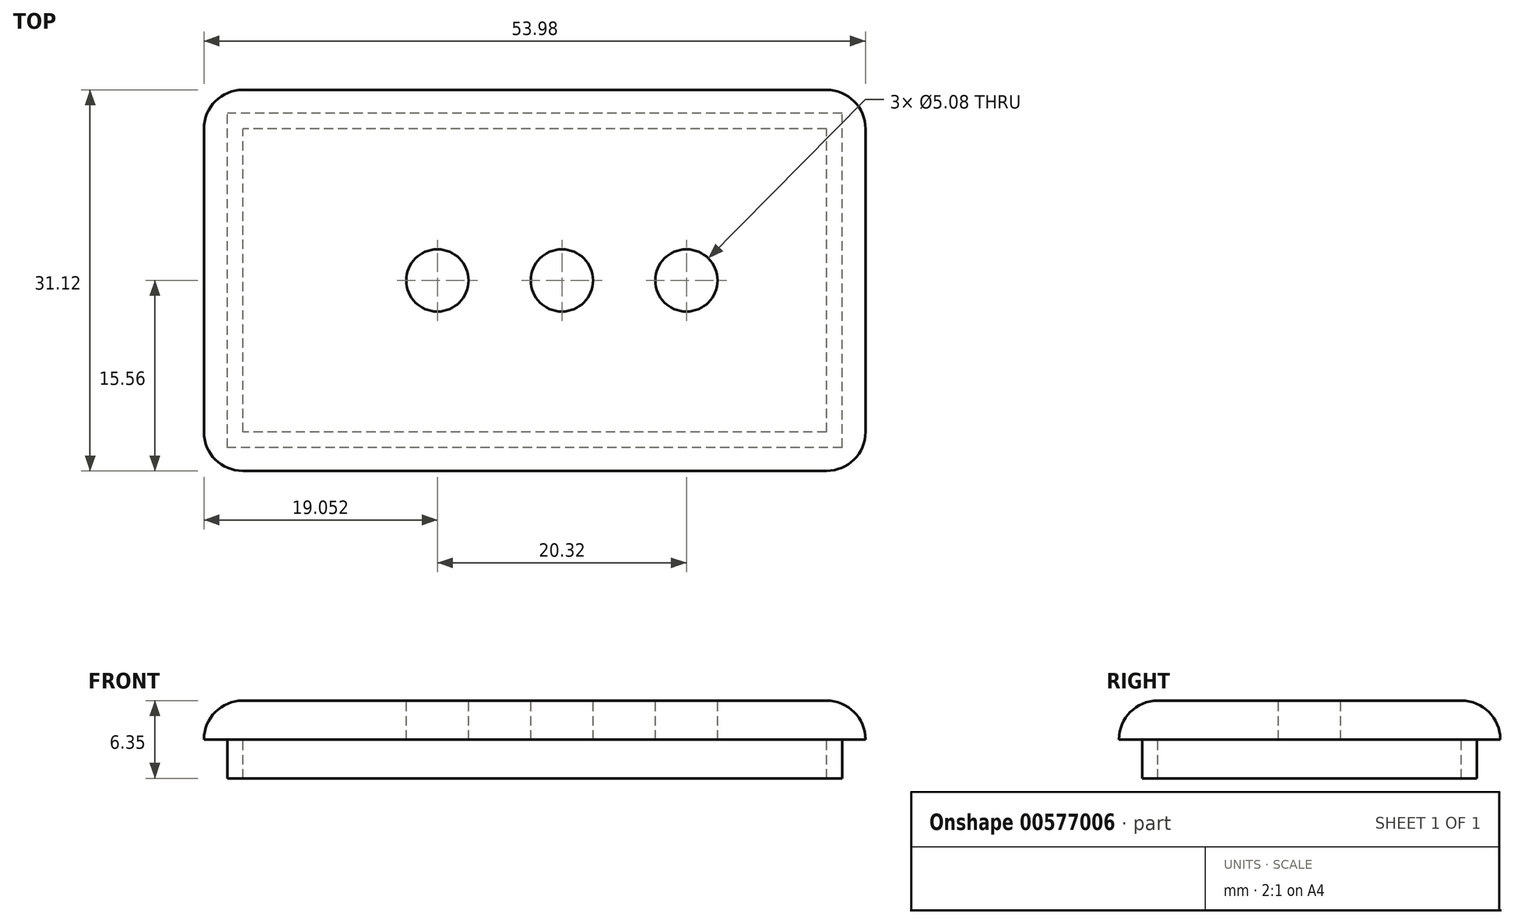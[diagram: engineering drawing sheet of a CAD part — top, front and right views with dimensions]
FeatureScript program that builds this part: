
annotation { "Feature Type Name" : "Feature", "Feature Type Description" : "" }
export const myFeature = defineFeature(function(context is Context, id is Id, definition is map)
    precondition{}
    {
        {
            var Q0;
            Q0=qCreatedBy(makeId("Top.planeOp"),FACE);
            var sketch = newSketch(context, id + "F0", { "sketchPlane" : qUnion([Q0])});
            skLineSegment(sketch, "E0.bottom", {"start": v(26.99, 15.56) * mm, "end": v(-26.99, 15.56) * mm});
            skLineSegment(sketch, "E0.top", {"start": v(26.99, -15.56) * mm, "end": v(-26.99, -15.56) * mm});
            skLineSegment(sketch, "E0.left", {"start": v(26.99, 15.56) * mm, "end": v(26.99, -15.56) * mm});
            skLineSegment(sketch, "E0.right", {"start": v(-26.99, 15.56) * mm, "end": v(-26.99, -15.56) * mm});
            skPoint(sketch, "E0.middle", {"position": v(0, 0) * mm});
            skSolve(sketch);
        }
        {
            var Q0;
            Q0 = qSketchRegion(id + "F0", true);
            extrude(context, id + "F1", {"entities" : qUnion([Q0]), "depth" : 3.17 * mm, "offsetDistance" : 25.4 * mm});
        }
        {
            var Q0;
            Q0=makeQuery(id+"F1.opExtrude","CAP_EDGE",EDGE,{"disambiguationData":[OSD([sQuery(id+"F0.wireOp",EDGE,"E0.top")])],"isStart":false});
            var Q1;
            Q1=makeQuery(id+"F1.opExtrude","CAP_EDGE",EDGE,{"disambiguationData":[OSD([sQuery(id+"F0.wireOp",EDGE,"E0.right")])],"isStart":false});
            var Q2;
            Q2=makeQuery(id+"F1.opExtrude","CAP_EDGE",EDGE,{"disambiguationData":[OSD([sQuery(id+"F0.wireOp",EDGE,"E0.bottom")])],"isStart":false});
            var Q3;
            Q3=makeQuery(id+"F1.opExtrude","CAP_EDGE",EDGE,{"disambiguationData":[OSD([sQuery(id+"F0.wireOp",EDGE,"E0.left")])],"isStart":false});
            var Q4;
            Q4=makeQuery(id+"F1.opExtrude","SWEPT_EDGE",EDGE,{"disambiguationData":[OSD([sQuery(id+"F0.wireOp",EDGE,"E0.top"),sQuery(id+"F0.wireOp",EDGE,"E0.left")])]});
            var Q5;
            Q5=makeQuery(id+"F1.opExtrude","SWEPT_EDGE",EDGE,{"disambiguationData":[OSD([sQuery(id+"F0.wireOp",EDGE,"E0.bottom"),sQuery(id+"F0.wireOp",EDGE,"E0.left")])]});
            var Q6;
            Q6=makeQuery(id+"F1.opExtrude","SWEPT_EDGE",EDGE,{"disambiguationData":[OSD([sQuery(id+"F0.wireOp",EDGE,"E0.bottom"),sQuery(id+"F0.wireOp",EDGE,"E0.right")])]});
            var Q7;
            Q7=makeQuery(id+"F1.opExtrude","SWEPT_EDGE",EDGE,{"disambiguationData":[OSD([sQuery(id+"F0.wireOp",EDGE,"E0.top"),sQuery(id+"F0.wireOp",EDGE,"E0.right")])]});
            fillet(context, id + "F2", {"entities" : qUnion([Q0, Q1, Q2, Q3, Q4, Q5, Q6, Q7]), "radius" : 3.17 * mm, "tangentPropagation" : true, "allowEdgeOverflow" : false});
        }
        {
            var Q0;
            Q0=makeQuery(id+"F1.opExtrude","CAP_FACE",FACE,{"disambiguationData":[OSD([sQuery(id+"F0.wireOp",EDGE,"E0.bottom"),sQuery(id+"F0.wireOp",EDGE,"E0.top"),sQuery(id+"F0.wireOp",EDGE,"E0.left"),sQuery(id+"F0.wireOp",EDGE,"E0.right")])],"isStart":true});
            var sketch = newSketch(context, id + "F3", { "sketchPlane" : qUnion([Q0])});
            skLineSegment(sketch, "E1.bottom", {"start": v(25.08, 13.65) * mm, "end": v(-25.08, 13.65) * mm});
            skLineSegment(sketch, "E1.top", {"start": v(25.08, -13.65) * mm, "end": v(-25.08, -13.65) * mm});
            skLineSegment(sketch, "E1.left", {"start": v(25.08, 13.65) * mm, "end": v(25.08, -13.65) * mm});
            skLineSegment(sketch, "E1.right", {"start": v(-25.08, 13.65) * mm, "end": v(-25.08, -13.65) * mm});
            skPoint(sketch, "E1.middle", {"position": v(0, 0) * mm});
            skLineSegment(sketch, "E2.bottom", {"start": v(23.81, 12.38) * mm, "end": v(-23.81, 12.38) * mm});
            skLineSegment(sketch, "E2.top", {"start": v(23.81, -12.38) * mm, "end": v(-23.81, -12.38) * mm});
            skLineSegment(sketch, "E2.left", {"start": v(23.81, 12.38) * mm, "end": v(23.81, -12.38) * mm});
            skLineSegment(sketch, "E2.right", {"start": v(-23.81, 12.38) * mm, "end": v(-23.81, -12.38) * mm});
            skSolve(sketch);
        }
        {
            var Q0;
            Q0 = qSketchRegion(id + "F3", true);
            var Q1;
            Q1=makeQuery(id+"F3.imprint","IMPRINT",FACE,{"disambiguationData":[TD([[makeQuery(id+"F3.imprint","IMPRINT",EDGE,{"derivedFrom":sQuery(id+"F3.wireOp",EDGE,"E1.bottom")}),1.0]])]});
            extrude(context, id + "F4", {"entities" : qUnion([Q0, Q1]), "operationType" : NewBodyOperationType.ADD, "depth" : 3.17 * mm, "offsetDistance" : 25.4 * mm});
        }
        {
            var Q0;
            Q0=makeQuery(id+"F1.opExtrude","CAP_FACE",FACE,{"disambiguationData":[OSD([sQuery(id+"F0.wireOp",EDGE,"E0.bottom"),sQuery(id+"F0.wireOp",EDGE,"E0.top"),sQuery(id+"F0.wireOp",EDGE,"E0.left"),sQuery(id+"F0.wireOp",EDGE,"E0.right")])],"isStart":false});
            var sketch = newSketch(context, id + "F5", { "sketchPlane" : qUnion([Q0])});
            skCircle(sketch, "E3", {"center": v(12.38, 0) * mm, "radius": 2.54 * mm});
            skCircle(sketch, "E4", {"center": v(2.22, 0) * mm, "radius": 2.54 * mm});
            skCircle(sketch, "E5", {"center": v(-7.94, 0) * mm, "radius": 2.54 * mm});
            skSolve(sketch);
        }
        {
            var Q0;
            Q0=sQuery(id+"F5.wireOp",VERTEX,"E5.center");
            var Q1;
            Q1=sQuery(id+"F5.wireOp",VERTEX,"E4.center");
            var Q2;
            Q2=sQuery(id+"F5.wireOp",VERTEX,"E3.center");
            var Q3;
            Q3=makeQuery(id+"F1.opExtrude","SWEPT_BODY",BODY,{"disambiguationData":[OSD([sQuery(id+"F0.wireOp",EDGE,"E0.bottom"),sQuery(id+"F0.wireOp",EDGE,"E0.top"),sQuery(id+"F0.wireOp",EDGE,"E0.left"),sQuery(id+"F0.wireOp",EDGE,"E0.right")])]});
            hole(context, id + "F6", {"style" : HoleStyle.SIMPLE, "endStyle" : HoleEndStyle.THROUGH, "holeDiameter" : 5.08 * mm, "isTappedThrough" : true, "tappedDepth" : 12.7 * mm, "tapClearance" : 3, "locations" : qUnion([Q0, Q1, Q2]), "scope" : qUnion([Q3])});
        }
    });
